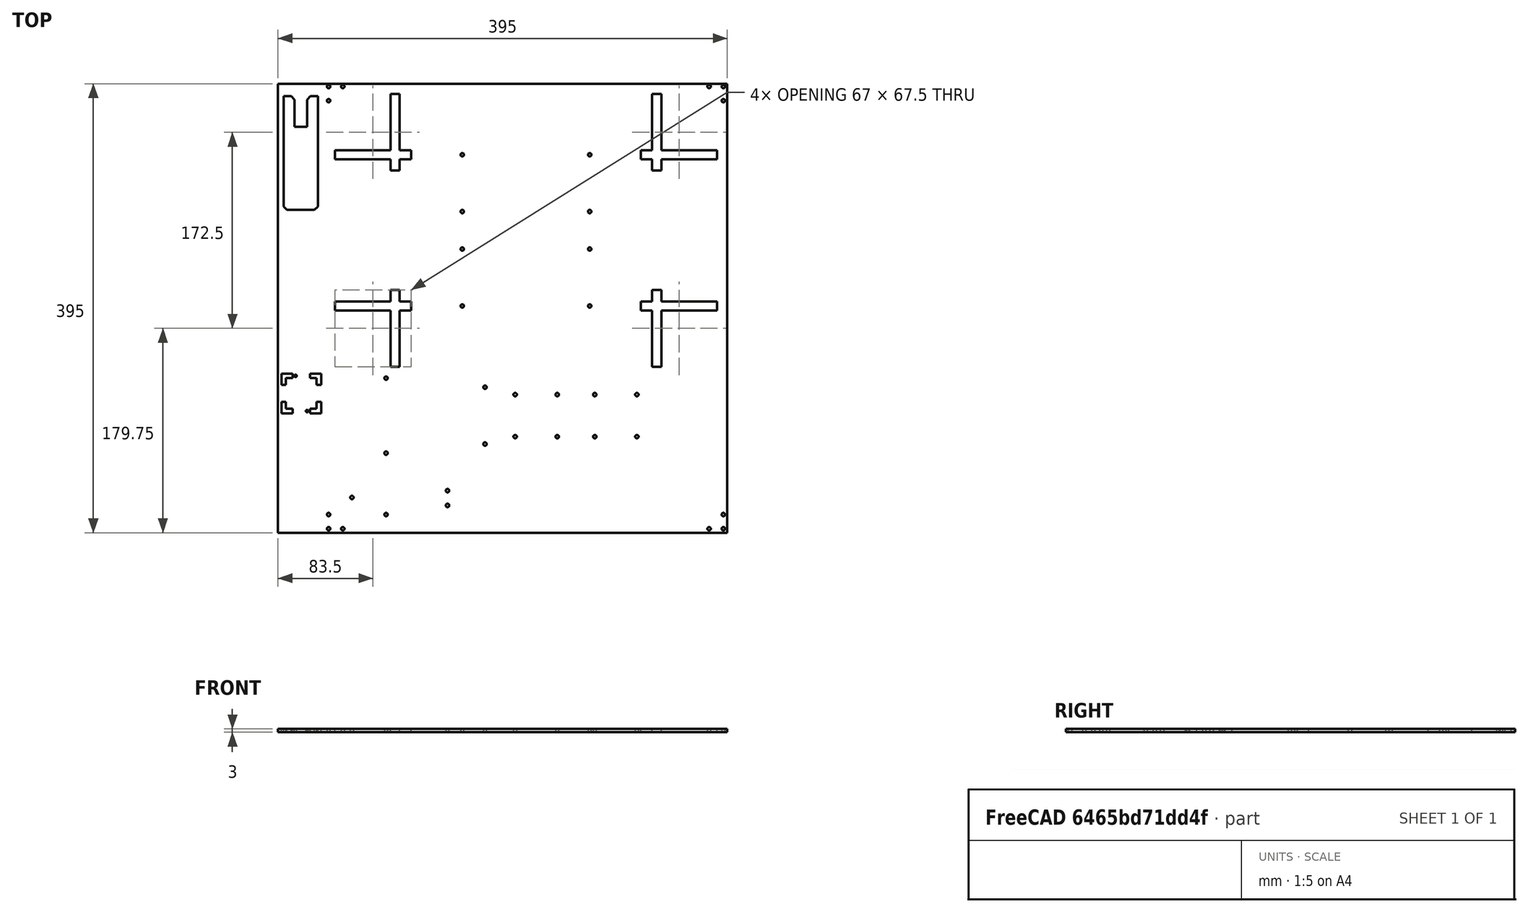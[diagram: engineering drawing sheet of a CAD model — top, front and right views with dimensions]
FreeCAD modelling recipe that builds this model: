
FCSTD DOCUMENT  (FreeCAD 0.19R24291 (Git))
Label: sibi_baseplate
License: All rights reserved
LicenseURL: http://en.wikipedia.org/wiki/All_rights_reserved
objects: Sketcher::SketchObject×1, Spreadsheet::Sheet×1, PartDesign::Pad×1, PartDesign::Body×1, App::Part×1, TechDraw::DrawSVGTemplate×1, TechDraw::DrawViewPart×1, TechDraw::DrawPage×1
note: 4 computed .brp shape members not serialized (recipe doc carries the construction recipe); baked Part::Feature solids carry a one-line shape summary decoded from their .brp

FEATURE [Sketcher::SketchObject] Sketch
  FullyConstrained = true
  MapMode = 5
  Support = -> [XY_Plane001]
  expr: Constraints[9] = <<Value_Spreadsheet>>.baseplate_size
  expr: Constraints[207] = 354.5 - 2.5 - 5
  expr: Constraints[39] = <<Value_Spreadsheet>>.vert_tab_length
  expr: Constraints[40] = <<Value_Spreadsheet>>.hor_tab_length
  expr: Constraints[122] = <<Value_Spreadsheet>>.vert_tab_length
  expr: Constraints[123] = <<Value_Spreadsheet>>.vert_tab_length
  expr: Constraints[121] = <<Value_Spreadsheet>>.hor_tab_length
  expr: Constraints[124] = <<Value_Spreadsheet>>.vert_tab_length
  expr: Constraints[125] = <<Value_Spreadsheet>>.hor_tab_length
  expr: Constraints[126] = <<Value_Spreadsheet>>.hor_tab_length
  sketch-geometry (136):
    g0: LineSegment StartX=-197.5 StartY=197.5 StartZ=0 EndX=197.5 EndY=197.5 EndZ=0
    g1: LineSegment StartX=197.5 StartY=197.5 StartZ=0 EndX=197.5 EndY=-197.5 EndZ=0
    g2: LineSegment StartX=197.5 StartY=-197.5 StartZ=0 EndX=-197.5 EndY=-197.5 EndZ=0
    g3: LineSegment StartX=-197.5 StartY=-197.5 StartZ=0 EndX=-197.5 EndY=197.5 EndZ=0
    g4: LineSegment StartX=-98.5 StartY=188.5 StartZ=0 EndX=-90.5 EndY=188.5 EndZ=0
    g5: LineSegment StartX=-90.5 StartY=188.5 StartZ=0 EndX=-90.5 EndY=139 EndZ=0
    g6: LineSegment StartX=-90.5 StartY=121 StartZ=0 EndX=-98.5 EndY=121 EndZ=0
    g7: LineSegment StartX=-98.5 StartY=121 StartZ=0 EndX=-98.5 EndY=131 EndZ=0
    g8: LineSegment StartX=-147.5 StartY=139 StartZ=0 EndX=-98.5 EndY=139 EndZ=0
    g9: LineSegment StartX=-80.5 StartY=139 StartZ=0 EndX=-80.5 EndY=131 EndZ=0
    g10: LineSegment StartX=-80.5 StartY=131 StartZ=0 EndX=-90.5 EndY=131 EndZ=0
    g11: LineSegment StartX=-147.5 StartY=131 StartZ=0 EndX=-147.5 EndY=139 EndZ=0
    g12: LineSegment StartX=-98.5 StartY=139 StartZ=0 EndX=-98.5 EndY=188.5 EndZ=0
    g13: LineSegment StartX=-90.5 StartY=131 StartZ=0 EndX=-90.5 EndY=121 EndZ=0
    g14: LineSegment StartX=-90.5 StartY=139 StartZ=0 EndX=-80.5 EndY=139 EndZ=0
    g15: LineSegment StartX=-98.5 StartY=131 StartZ=0 EndX=-147.5 EndY=131 EndZ=0
    g16: LineSegment StartX=121.5 StartY=139 StartZ=0 EndX=131.5 EndY=139 EndZ=0
    g17: LineSegment StartX=188.5 StartY=139 StartZ=0 EndX=188.5 EndY=131 EndZ=0
    g18: LineSegment StartX=188.5 StartY=131 StartZ=0 EndX=139.5 EndY=131 EndZ=0
    g19: LineSegment StartX=121.5 StartY=131 StartZ=0 EndX=121.5 EndY=139 EndZ=0
    g20: LineSegment StartX=131.5 StartY=188.5 StartZ=0 EndX=139.5 EndY=188.5 EndZ=0
    g21: LineSegment StartX=139.5 StartY=188.5 StartZ=0 EndX=139.5 EndY=139 EndZ=0
    g22: LineSegment StartX=139.5 StartY=121 StartZ=0 EndX=131.5 EndY=121 EndZ=0
    g23: LineSegment StartX=131.5 StartY=121 StartZ=0 EndX=131.5 EndY=131 EndZ=0
    g24: LineSegment StartX=-98.5 StartY=16 StartZ=0 EndX=-90.5 EndY=16 EndZ=0
    g25: LineSegment StartX=-90.5 StartY=16 StartZ=0 EndX=-90.5 EndY=6 EndZ=0
    g26: LineSegment StartX=-90.5 StartY=-51.5 StartZ=0 EndX=-98.5 EndY=-51.5 EndZ=0
    g27: LineSegment StartX=-98.5 StartY=-51.5 StartZ=0 EndX=-98.5 EndY=-2 EndZ=0
    g28: LineSegment StartX=-80.5 StartY=6 StartZ=0 EndX=-90.5 EndY=6 EndZ=0
    g29: LineSegment StartX=-147.5 StartY=6 StartZ=0 EndX=-147.5 EndY=-2 EndZ=0
    g30: LineSegment StartX=-147.5 StartY=-2 StartZ=0 EndX=-98.5 EndY=-2 EndZ=0
    g31: LineSegment StartX=-80.5 StartY=-2 StartZ=0 EndX=-80.5 EndY=6 EndZ=0
    g32: LineSegment StartX=131.5 StartY=16 StartZ=0 EndX=139.5 EndY=16 EndZ=0
    g33: LineSegment StartX=139.5 StartY=16 StartZ=0 EndX=139.5 EndY=6 EndZ=0
    g34: LineSegment StartX=139.5 StartY=-51.5 StartZ=0 EndX=131.5 EndY=-51.5 EndZ=0
    g35: LineSegment StartX=131.5 StartY=-51.5 StartZ=0 EndX=131.5 EndY=-2 EndZ=0
    g36: LineSegment StartX=121.5 StartY=6 StartZ=0 EndX=131.5 EndY=6 EndZ=0
    g37: LineSegment StartX=188.5 StartY=6 StartZ=0 EndX=188.5 EndY=-2 EndZ=0
    g38: LineSegment StartX=188.5 StartY=-2 StartZ=0 EndX=139.5 EndY=-2 EndZ=0
    g39: LineSegment StartX=121.5 StartY=-2 StartZ=0 EndX=121.5 EndY=6 EndZ=0
    g40: LineSegment StartX=139.5 StartY=139 StartZ=0 EndX=188.5 EndY=139 EndZ=0
    g41: LineSegment StartX=131.5 StartY=139 StartZ=0 EndX=131.5 EndY=188.5 EndZ=0
    g42: LineSegment StartX=131.5 StartY=131 StartZ=0 EndX=121.5 EndY=131 EndZ=0
    g43: LineSegment StartX=139.5 StartY=131 StartZ=0 EndX=139.5 EndY=121 EndZ=0
    g44: LineSegment StartX=139.5 StartY=6 StartZ=0 EndX=188.5 EndY=6 EndZ=0
    g45: LineSegment StartX=131.5 StartY=6 StartZ=0 EndX=131.5 EndY=16 EndZ=0
    g46: LineSegment StartX=131.5 StartY=-2 StartZ=0 EndX=121.5 EndY=-2 EndZ=0
    g47: LineSegment StartX=139.5 StartY=-2 StartZ=0 EndX=139.5 EndY=-51.5 EndZ=0
    g48: LineSegment StartX=-98.5 StartY=6 StartZ=0 EndX=-147.5 EndY=6 EndZ=0
    g49: LineSegment StartX=-98.5 StartY=6 StartZ=0 EndX=-98.5 EndY=16 EndZ=0
    g50: LineSegment StartX=-90.5 StartY=-2 StartZ=0 EndX=-80.5 EndY=-2 EndZ=0
    g51: LineSegment StartX=-90.5 StartY=-2 StartZ=0 EndX=-90.5 EndY=-51.5 EndZ=0
    g52: Circle CenterX=194 CenterY=195 CenterZ=0 NormalX=0 NormalY=0 NormalZ=1 AngleXU=0 Radius=1.5
    g53: Circle CenterX=181.5 CenterY=195 CenterZ=0 NormalX=0 NormalY=0 NormalZ=1 AngleXU=0 Radius=1.5
    g54: Circle CenterX=194 CenterY=182.5 CenterZ=0 NormalX=0 NormalY=0 NormalZ=1 AngleXU=0 Radius=1.5
    g55: Circle CenterX=194 CenterY=-181.5 CenterZ=0 NormalX=0 NormalY=0 NormalZ=1 AngleXU=0 Radius=1.5
    g56: Circle CenterX=194 CenterY=-194 CenterZ=0 NormalX=0 NormalY=0 NormalZ=1 AngleXU=0 Radius=1.5
    g57: Circle CenterX=181.5 CenterY=-194 CenterZ=0 NormalX=0 NormalY=0 NormalZ=1 AngleXU=0 Radius=1.5
    g58: Circle CenterX=-102.5 CenterY=-61.5 CenterZ=0 NormalX=0 NormalY=0 NormalZ=1 AngleXU=0 Radius=1.5
    g59: Circle CenterX=-102.5 CenterY=-127.5 CenterZ=0 NormalX=0 NormalY=0 NormalZ=1 AngleXU=0 Radius=1.5
    g60: Circle CenterX=-15.5 CenterY=-69.5 CenterZ=0 NormalX=0 NormalY=0 NormalZ=1 AngleXU=0 Radius=1.5
    g61: Circle CenterX=-15.5 CenterY=-119.5 CenterZ=0 NormalX=0 NormalY=0 NormalZ=1 AngleXU=0 Radius=1.5
    g62: GeomPoint X=-102.5 Y=-94.5 Z=0
    g63: GeomPoint X=-15.5 Y=-94.5 Z=0
    g64: Circle CenterX=11 CenterY=-76 CenterZ=0 NormalX=0 NormalY=0 NormalZ=1 AngleXU=0 Radius=1.5
    g65: Circle CenterX=11 CenterY=-113 CenterZ=0 NormalX=0 NormalY=0 NormalZ=1 AngleXU=0 Radius=1.5
    g66: Circle CenterX=48 CenterY=-76 CenterZ=0 NormalX=0 NormalY=0 NormalZ=1 AngleXU=0 Radius=1.5
    g67: Circle CenterX=48 CenterY=-113 CenterZ=0 NormalX=0 NormalY=0 NormalZ=1 AngleXU=0 Radius=1.5
    g68: Circle CenterX=81 CenterY=-76 CenterZ=0 NormalX=0 NormalY=0 NormalZ=1 AngleXU=0 Radius=1.5
    g69: Circle CenterX=118 CenterY=-76 CenterZ=0 NormalX=0 NormalY=0 NormalZ=1 AngleXU=0 Radius=1.5
    g70: Circle CenterX=81 CenterY=-113 CenterZ=0 NormalX=0 NormalY=0 NormalZ=1 AngleXU=0 Radius=1.5
    g71: Circle CenterX=118 CenterY=-113 CenterZ=0 NormalX=0 NormalY=0 NormalZ=1 AngleXU=0 Radius=1.5
    g72: GeomPoint X=29.5 Y=-94.5 Z=0
    g73: GeomPoint X=99.5 Y=-94.5 Z=0
    g74: Circle CenterX=-48.5 CenterY=-160.5 CenterZ=0 NormalX=0 NormalY=0 NormalZ=1 AngleXU=0 Radius=1.5
    g75: Circle CenterX=-48.5 CenterY=-173.5 CenterZ=0 NormalX=0 NormalY=0 NormalZ=1 AngleXU=0 Radius=1.5
    g76: Circle CenterX=-153 CenterY=195 CenterZ=0 NormalX=0 NormalY=0 NormalZ=1 AngleXU=0 Radius=1.5
    g77: Circle CenterX=-140.5 CenterY=195 CenterZ=0 NormalX=0 NormalY=0 NormalZ=1 AngleXU=0 Radius=1.5
    g78: Circle CenterX=-153 CenterY=182.5 CenterZ=0 NormalX=0 NormalY=0 NormalZ=1 AngleXU=0 Radius=1.5
    g79: Circle CenterX=-153 CenterY=-194 CenterZ=0 NormalX=0 NormalY=0 NormalZ=1 AngleXU=0 Radius=1.5
    g80: Circle CenterX=-153 CenterY=-181.5 CenterZ=0 NormalX=0 NormalY=0 NormalZ=1 AngleXU=0 Radius=1.5
    g81: Circle CenterX=-140.5 CenterY=-194 CenterZ=0 NormalX=0 NormalY=0 NormalZ=1 AngleXU=0 Radius=1.5
    g82: GeomPoint X=-80.5 Y=135 Z=0
    g83: GeomPoint X=121.5 Y=135 Z=0
    g84: Circle CenterX=-35.5 CenterY=135 CenterZ=0 NormalX=0 NormalY=0 NormalZ=1 AngleXU=0 Radius=1.5
    g85: Circle CenterX=76.5 CenterY=135 CenterZ=0 NormalX=0 NormalY=0 NormalZ=1 AngleXU=0 Radius=1.5
    g86: Circle CenterX=-35.5 CenterY=2 CenterZ=0 NormalX=0 NormalY=0 NormalZ=1 AngleXU=0 Radius=1.5
    g87: Circle CenterX=76.5 CenterY=2 CenterZ=0 NormalX=0 NormalY=0 NormalZ=1 AngleXU=0 Radius=1.5
    g88: GeomPoint X=20.5 Y=135 Z=0
    g89: GeomPoint X=-80.5 Y=2 Z=0
    g90: GeomPoint X=121.5 Y=2 Z=0
    g91: GeomPoint X=20.5 Y=2 Z=0
    g92: LineSegment StartX=-159.5 StartY=-57.5 StartZ=0 EndX=-159.5 EndY=-47.5 EndZ=0
    g93: LineSegment StartX=-159.5 StartY=-47.5 StartZ=0 EndX=-163.5 EndY=-47.5 EndZ=0
    g94: LineSegment StartX=-163.5 StartY=-47.5 StartZ=0 EndX=-163.5 EndY=-61.5 EndZ=0
    g95: LineSegment StartX=-163.5 StartY=-61.5 StartZ=0 EndX=-169.5 EndY=-61.5 EndZ=0
    g96: LineSegment StartX=-169.5 StartY=-61.5 StartZ=0 EndX=-169.5 EndY=-57.5 EndZ=0
    g97: LineSegment StartX=-169.5 StartY=-57.5 StartZ=0 EndX=-159.5 EndY=-57.5 EndZ=0
    g98: LineSegment StartX=-184.5 StartY=-53.5 StartZ=0 EndX=-184.5 EndY=-57.5 EndZ=0
    g99: LineSegment StartX=-184.5 StartY=-57.5 StartZ=0 EndX=-194.5 EndY=-57.5 EndZ=0
    g100: LineSegment StartX=-194.5 StartY=-57.5 StartZ=0 EndX=-194.5 EndY=-47.5 EndZ=0
    g101: LineSegment StartX=-194.5 StartY=-47.5 StartZ=0 EndX=-190.5 EndY=-47.5 EndZ=0
    g102: LineSegment StartX=-190.5 StartY=-47.5 StartZ=0 EndX=-190.5 EndY=-53.5 EndZ=0
    g103: LineSegment StartX=-190.5 StartY=-53.5 StartZ=0 EndX=-184.5 EndY=-53.5 EndZ=0
    g104: LineSegment StartX=-194.5 StartY=-32.5 StartZ=0 EndX=-190.5 EndY=-32.5 EndZ=0
    g105: LineSegment StartX=-190.5 StartY=-32.5 StartZ=0 EndX=-190.5 EndY=-26.5 EndZ=0
    g106: LineSegment StartX=-190.5 StartY=-26.5 StartZ=0 EndX=-184.5 EndY=-26.5 EndZ=0
    g107: LineSegment StartX=-184.5 StartY=-26.5 StartZ=0 EndX=-184.5 EndY=-22.5 EndZ=0
    g108: LineSegment StartX=-184.5 StartY=-22.5 StartZ=0 EndX=-194.5 EndY=-22.5 EndZ=0
    g109: LineSegment StartX=-194.5 StartY=-22.5 StartZ=0 EndX=-194.5 EndY=-32.5 EndZ=0
    g110: LineSegment StartX=-169.5 StartY=-22.5 StartZ=0 EndX=-159.5 EndY=-22.5 EndZ=0
    g111: LineSegment StartX=-159.5 StartY=-22.5 StartZ=0 EndX=-159.5 EndY=-32.5 EndZ=0
    g112: LineSegment StartX=-159.5 StartY=-32.5 StartZ=0 EndX=-163.5 EndY=-32.5 EndZ=0
    g113: LineSegment StartX=-163.5 StartY=-32.5 StartZ=0 EndX=-163.5 EndY=-26.5 EndZ=0
    g114: LineSegment StartX=-163.5 StartY=-26.5 StartZ=0 EndX=-169.5 EndY=-26.5 EndZ=0
    g115: LineSegment StartX=-169.5 StartY=-26.5 StartZ=0 EndX=-169.5 EndY=-22.5 EndZ=0
    g116: Circle CenterX=-172 CenterY=-63.5 CenterZ=0 NormalX=0 NormalY=0 NormalZ=1 AngleXU=0 Radius=1
    g117: Circle CenterX=-182 CenterY=-24.5 CenterZ=0 NormalX=0 NormalY=0 NormalZ=1 AngleXU=0 Radius=1
    g118: Circle CenterX=-35.5 CenterY=85 CenterZ=0 NormalX=0 NormalY=0 NormalZ=1 AngleXU=0 Radius=1.5
    g119: Circle CenterX=-35.5 CenterY=52 CenterZ=0 NormalX=0 NormalY=0 NormalZ=1 AngleXU=0 Radius=1.5
    g120: Circle CenterX=76.5 CenterY=85 CenterZ=0 NormalX=0 NormalY=0 NormalZ=1 AngleXU=0 Radius=1.5
    g121: Circle CenterX=76.5 CenterY=52 CenterZ=0 NormalX=0 NormalY=0 NormalZ=1 AngleXU=0 Radius=1.5
    g122: LineSegment StartX=-192.5 StartY=186.5 StartZ=0 EndX=-192.5 EndY=89.5 EndZ=0
    g123: LineSegment StartX=-192.5 StartY=89.5 StartZ=0 EndX=-189.5 EndY=86.5 EndZ=0
    g124: LineSegment StartX=-189.5 StartY=86.5 StartZ=0 EndX=-165.5 EndY=86.5 EndZ=0
    g125: LineSegment StartX=-165.5 StartY=86.5 StartZ=0 EndX=-162.5 EndY=89.5 EndZ=0
    g126: LineSegment StartX=-162.5 StartY=89.5 StartZ=0 EndX=-162.5 EndY=186.5 EndZ=0
    g127: LineSegment StartX=-162.5 StartY=186.5 StartZ=0 EndX=-169 EndY=186.5 EndZ=0
    g128: LineSegment StartX=-169 StartY=186.5 StartZ=0 EndX=-172 EndY=183.5 EndZ=0
    g129: LineSegment StartX=-172 StartY=183.5 StartZ=0 EndX=-172 EndY=159.5 EndZ=0
    g130: LineSegment StartX=-172 StartY=159.5 StartZ=0 EndX=-183 EndY=159.5 EndZ=0
    g131: LineSegment StartX=-183 StartY=159.5 StartZ=0 EndX=-183 EndY=183.5 EndZ=0
    g132: LineSegment StartX=-183 StartY=183.5 StartZ=0 EndX=-186 EndY=186.5 EndZ=0
    g133: LineSegment StartX=-186 StartY=186.5 StartZ=0 EndX=-192.5 EndY=186.5 EndZ=0
    g134: Circle CenterX=-132.5 CenterY=-166.5 CenterZ=0 NormalX=0 NormalY=0 NormalZ=1 AngleXU=0 Radius=1.5
    g135: Circle CenterX=-102.5 CenterY=-181.5 CenterZ=0 NormalX=0 NormalY=0 NormalZ=1 AngleXU=0 Radius=1.5
  constraints (365):
    c: Coincident(g0,g1)
    c: Coincident(g1,g2)
    c: Coincident(g2,g3)
    c: Coincident(g3,g0)
    c: Horizontal(g0)
    c: Horizontal(g2)
    c: Vertical(g1)
    c: Vertical(g3)
    c: Equal(g0,g3)
    c: DistanceX(g0,g0) = 395
    c: Symmetric(g0,g1,g-1)
    c: Coincident(g4,g5)
    c: Coincident(g13,g6)
    c: Coincident(g6,g7)
    c: Coincident(g12,g4)
    c: Horizontal(g4)
    c: Horizontal(g6)
    c: Vertical(g5)
    c: Vertical(g7)
    c: Coincident(g14,g9)
    c: Coincident(g9,g10)
    c: Coincident(g15,g11)
    c: Coincident(g11,g8)
    c: Horizontal(g8)
    c: Horizontal(g10)
    c: Vertical(g9)
    c: Vertical(g11)
    c: Tangent(g7,g12)
    c: Tangent(g5,g13)
    c: Coincident(g8,g12)
    c: Coincident(g14,g5)
    c: Tangent(g8,g14)
    c: Coincident(g10,g13)
    c: Coincident(g15,g7)
    c: Tangent(g10,g15)
    c: Equal(g13,g10)
    c: DistanceX(g10,g10) = 10
    c: Equal(g6,g9)
    c: DistanceY(g11,g11) = 8
    c: DistanceY(g6,g4) = 67.5
    c: DistanceX(g11,g9) = 67
    c: Coincident(g40,g17)
    c: Coincident(g17,g18)
    c: Coincident(g42,g19)
    c: Coincident(g19,g16)
    c: Horizontal(g16)
    c: Horizontal(g18)
    c: Vertical(g17)
    c: Vertical(g19)
    c: Coincident(g20,g21)
    c: Coincident(g43,g22)
    c: Coincident(g22,g23)
    c: Coincident(g41,g20)
    c: Vertical(g21)
    c: Vertical(g23)
    c: Coincident(g24,g25)
    c: Coincident(g51,g26)
    c: Coincident(g26,g27)
    c: Coincident(g49,g24)
    c: Horizontal(g24)
    c: Horizontal(g26)
    c: Vertical(g25)
    c: Vertical(g27)
    c: Coincident(g48,g29)
    c: Coincident(g29,g30)
    c: Coincident(g50,g31)
    c: Coincident(g31,g28)
    c: Horizontal(g28)
    c: Horizontal(g30)
    c: Coincident(g32,g33)
    c: Coincident(g47,g34)
    c: Coincident(g34,g35)
    c: Coincident(g45,g32)
    c: Vertical(g33)
    c: Vertical(g35)
    c: Coincident(g44,g37)
    c: Coincident(g37,g38)
    c: Coincident(g46,g39)
    c: Coincident(g39,g36)
    c: Horizontal(g36)
    c: Horizontal(g38)
    c: Tangent(g16,g40)
    c: Coincident(g41,g16)
    c: Tangent(g23,g41)
    c: Coincident(g42,g23)
    c: Tangent(g18,g42)
    c: Coincident(g21,g40)
    c: Coincident(g43,g18)
    c: Tangent(g21,g43)
    c: Tangent(g36,g44)
    c: Coincident(g45,g36)
    c: Tangent(g35,g45)
    c: Coincident(g46,g35)
    c: Tangent(g38,g46)
    c: Coincident(g33,g44)
    c: Coincident(g47,g38)
    c: Tangent(g33,g47)
    c: Tangent(g28,g48)
    c: Coincident(g49,g48)
    c: Tangent(g27,g49)
    c: Coincident(g30,g27)
    c: Tangent(g30,g50)
    c: Coincident(g25,g28)
    c: Coincident(g51,g50)
    c: Tangent(g25,g51)
    c: Equal(g13,g25)
    c: Equal(g28,g25)
    c: Equal(g45,g36)
    c: Equal(g45,g10)
    c: Equal(g42,g23)
    c: Equal(g42,g10)
    c: Equal(g9,g19)
    c: Equal(g19,g22)
    c: Equal(g32,g39)
    c: Equal(g22,g32)
    c: Equal(g31,g24)
    c: Equal(g24,g6)
    c: Tangent(g9,g31)
    c: Tangent(g6,g22)
    c: Tangent(g39,g19)
    c: Tangent(g24,g32)
    c: DistanceX(g19,g17) = 67
    c: DistanceY(g22,g20) = 67.5
    c: DistanceY(g34,g32) = 67.5
    c: DistanceY(g26,g24) = 67.5
    c: DistanceX(g29,g28) = 67
    c: DistanceX(g36,g37) = 67
    c: DistanceX(g9,g19) = 202
    c: Vertical(g37)
    c: DistanceY(g24,g6) = 105
    c: Horizontal(g20)
    c: Horizontal(g34)
    c: DistanceX(g0,g17) = -9
    c: Vertical(g29)
    c: DistanceY(g20,g0) = 9
    c: Equal(g53,g52)
    c: Equal(g52,g54)
    c: Diameter(g52) = 3
    c: DistanceY(g53,g52) = 0
    c: DistanceY(g54,g52) = 12.5
    c: DistanceX(g54,g52) = 0
    c: DistanceX(g53,g52) = 12.5
    c: DistanceX(g52,g0) = 3.5
    c: DistanceY(g52,g0) = 2.5
    c: Equal(g57,g56)
    c: Equal(g56,g55)
    c: Equal(g56,g52)
    c: DistanceX(g57,g56) = 12.5
    c: DistanceX(g56,g55) = 0
    c: DistanceY(g57,g56) = 0
    c: DistanceY(g56,g55) = 12.5
    c: DistanceY(g1,g56) = 3.5
    c: DistanceY(g63,g62) = 0
    c: DistanceX(g62,g63) = 87
    c: Symmetric(g58,g59,g62)
    c: Symmetric(g60,g61,g63)
    c: DistanceX(g59,g58) = 0
    c: DistanceX(g60,g61) = 0
    c: DistanceY(g61,g60) = 50
    c: DistanceY(g59,g58) = 66
    c: DistanceY(g2,g59) = 70
    c: DistanceX(g2,g59) = 95
    c: Equal(g58,g59)
    c: Equal(g58,g61)
    c: Equal(g58,g60)
    c: Diameter(g58) = 3
    c: DistanceX(g64,g66) = 37
    c: DistanceX(g65,g64) = 0
    c: DistanceX(g66,g67) = 0
    c: DistanceY(g64,g66) = 0
    c: DistanceY(g67,g65) = 0
    c: DistanceY(g67,g66) = 37
    c: Equal(g64,g66)
    c: Equal(g64,g67)
    c: Equal(g64,g65)
    c: Diameter(g64) = 3
    c: DistanceY(g68,g69) = 0
    c: DistanceY(g71,g70) = 0
    c: DistanceY(g70,g68) = 37
    c: DistanceX(g70,g68) = 0
    c: DistanceX(g71,g69) = 0
    c: DistanceX(g68,g69) = 37
    c: Equal(g64,g68)
    c: Equal(g68,g69)
    c: Equal(g68,g71)
    c: Equal(g68,g70)
    c: Symmetric(g66,g65,g72)
    c: Symmetric(g70,g69,g73)
    c: DistanceY(g73,g72) = 0
    c: DistanceY(g63,g72) = 0
    c: DistanceX(g63,g72) = 45
    c: DistanceX(g72,g73) = 70
    c: DistanceX(g75,g74) = 0
    c: DistanceY(g75,g74) = 13
    c: DistanceY(g2,g75) = 24
    c: DistanceX(g74,g1) = 246
    c: Equal(g74,g75)
    c: Diameter(g74) = 3
    c: Equal(g76,g77)
    c: Equal(g77,g78)
    c: Equal(g76,g52)
    c: DistanceY(g77,g76) = 0
    c: DistanceY(g78,g76) = 12.5
    c: DistanceX(g76,g78) = 0
    c: DistanceX(g76,g77) = 12.5
    c: DistanceX(g52,g56) = 0
    c: DistanceY(g76,g52) = 0
    c: DistanceX(g76,g52) = 347
    c: Equal(g80,g79)
    c: Equal(g79,g81)
    c: Equal(g81,g52)
    c: DistanceX(g80,g79) = 0
    c: DistanceX(g79,g81) = 12.5
    c: DistanceX(g76,g79) = 0
    c: DistanceY(g81,g79) = 0
    c: DistanceY(g79,g80) = 12.5
    c: DistanceY(g56,g79) = 0
    c: Symmetric(g9,g9,g82)
    c: Symmetric(g16,g19,g83)
    c: Equal(g84,g85)
    c: Equal(g85,g86)
    c: Equal(g86,g87)
    c: Equal(g87,g52)
    c: DistanceY(g84,g85) = 0
    c: Symmetric(g83,g82,g88)
    c: Symmetric(g84,g85,g88)
    c: DistanceX(g9,g84) = 45
    c: Symmetric(g28,g31,g89)
    c: Symmetric(g36,g39,g90)
    c: Symmetric(g90,g89,g91)
    c: Symmetric(g86,g87,g91)
    c: DistanceY(g87,g86) = 0
    c: DistanceX(g86,g84) = 0
    c: Vertical(g92)
    c: Coincident(g92,g93)
    c: Horizontal(g93)
    c: Coincident(g93,g94)
    c: Vertical(g94)
    c: Coincident(g94,g95)
    c: Horizontal(g95)
    c: Coincident(g95,g96)
    c: Vertical(g96)
    c: Coincident(g96,g97)
    c: Coincident(g97,g92)
    c: Horizontal(g97)
    c: DistanceX(g93,g93) = 4
    c: Equal(g96,g93)
    c: DistanceY(g92,g92) = 10
    c: Equal(g97,g92)
    c: DistanceY(g2,g96) = 140
    c: DistanceX(g2,g92) = 38
    c: Vertical(g98)
    c: Coincident(g98,g99)
    c: Horizontal(g99)
    c: Coincident(g99,g100)
    c: Vertical(g100)
    c: Coincident(g100,g101)
    c: Horizontal(g101)
    c: Coincident(g101,g102)
    c: Vertical(g102)
    c: Coincident(g102,g103)
    c: Coincident(g103,g98)
    c: Horizontal(g103)
    c: Equal(g101,g93)
    c: Equal(g99,g92)
    c: Equal(g100,g99)
    c: Equal(g101,g98)
    c: DistanceY(g92,g99) = 0
    c: DistanceX(g99,g92) = 35
    c: Horizontal(g104)
    c: Coincident(g104,g105)
    c: Vertical(g105)
    c: Coincident(g105,g106)
    c: Horizontal(g106)
    c: Coincident(g106,g107)
    c: Vertical(g107)
    c: Coincident(g107,g108)
    c: Horizontal(g108)
    c: Coincident(g108,g109)
    c: Coincident(g109,g104)
    c: Vertical(g109)
    c: Equal(g109,g92)
    c: Equal(g108,g92)
    c: Equal(g93,g104)
    c: Equal(g93,g107)
    c: DistanceX(g108,g99) = 0
    c: DistanceY(g99,g108) = 35
    c: Horizontal(g110)
    c: Coincident(g110,g111)
    c: Vertical(g111)
    c: Coincident(g111,g112)
    c: Horizontal(g112)
    c: Coincident(g112,g113)
    c: Vertical(g113)
    c: Coincident(g113,g114)
    c: Horizontal(g114)
    c: Coincident(g114,g115)
    c: Coincident(g115,g110)
    c: Vertical(g115)
    c: Equal(g112,g93)
    c: Equal(g115,g93)
    c: Equal(g111,g92)
    c: Equal(g92,g110)
    c: DistanceX(g92,g110) = 0
    c: DistanceY(g108,g110) = 0
    c: DistanceY(g116,g95) = 2
    c: DistanceX(g116,g95) = 2.5
    c: Diameter(g116) = 2
    c: Diameter(g117) = 2
    c: DistanceY(g117,g107) = 2
    c: DistanceX(g107,g117) = 2.5
    c: Diameter(g118) = 3
    c: Equal(g119,g118)
    c: Equal(g121,g118)
    c: Equal(g120,g118)
    c: DistanceX(g118,g84) = 0
    c: DistanceX(g119,g118) = 0
    c: DistanceY(g118,g84) = 50
    c: DistanceY(g86,g119) = 50
    c: DistanceY(g121,g119) = 0
    c: DistanceY(g118,g120) = 0
    c: DistanceX(g121,g87) = 0
    c: DistanceX(g120,g121) = 0
    c: Vertical(g122)
    c: Coincident(g122,g123)
    c: Coincident(g123,g124)
    c: Horizontal(g124)
    c: Coincident(g124,g125)
    c: Coincident(g125,g126)
    c: Vertical(g126)
    c: Coincident(g126,g127)
    c: Horizontal(g127)
    c: Coincident(g127,g128)
    c: Coincident(g128,g129)
    c: Vertical(g129)
    c: Coincident(g129,g130)
    c: Horizontal(g130)
    c: Coincident(g130,g131)
    c: Vertical(g131)
    c: Coincident(g131,g132)
    c: Coincident(g132,g133)
    c: Coincident(g133,g122)
    c: Horizontal(g133)
    c: DistanceY(g122,g0) = 11
    c: DistanceX(g0,g122) = 5
    c: DistanceX(g133,g133) = 6.5
    c: Equal(g133,g127)
    c: DistanceY(g122,g122) = 97
    c: Equal(g122,g126)
    c: DistanceY(g122,g126) = 0
    c: DistanceX(g124,g124) = 24
    c: Equal(g125,g123)
    c: DistanceY(g123,g122) = 3
    c: Equal(g132,g128)
    c: DistanceY(g131,g131) = 24
    c: Equal(g131,g129)
    c: DistanceX(g130,g130) = 11
    c: DistanceX(g122,g126) = 30
    c: DistanceY(g128,g127) = 3
    c: Diameter(g134) = 3
    c: Equal(g134,g135)
    c: DistanceX(g134,g135) = 30
    c: DistanceY(g135,g134) = 15
    c: DistanceX(g59,g135) = 0
    c: DistanceY(g80,g135) = 0
FEATURE [Spreadsheet::Sheet] Spreadsheet  label="Value_Spreadsheet"
  cells = A2=Baseplate Width; B2(baseplate_size)=395; A5=Horizontal Tab; B5(hor_tab_length)=67; A6=Vertical Tab; B6(vert_tab_length)=67.5
FEATURE [PartDesign::Pad] Pad
  Direction = (1,1,1)
  Length = 3
  Length2 = 100
  Profile = -> Sketch
  Refine = true
  Type = 0
FEATURE [PartDesign::Body] Body
  Group = -> [Sketch,Pad]
  Origin = -> Origin001
  Placement = pos=(200,-200,0) rot=(0,0,1;0rad)
  Tip = -> Pad
FEATURE [App::Part] Part
  Group = -> [Body]
  Origin = -> Origin
FEATURE [TechDraw::DrawSVGTemplate] Template
  Height = 420
  Orientation = 1
  Width = 594
FEATURE [TechDraw::DrawViewPart] View
  CoarseView = false
  Direction = (0,0,1)
  Focus = 100
  HardHidden = false
  IsoCount = 0
  IsoHidden = false
  IsoVisible = false
  LockPosition = false
  Perspective = false
  Rotation = 0
  ScaleType = 0
  SeamHidden = false
  SeamVisible = true
  SmoothHidden = false
  SmoothVisible = true
  Source = -> [Sketch]
  X = 297
  XDirection = (1,0,0)
  Y = 210
FEATURE [TechDraw::DrawPage] Page
  KeepUpdated = true
  NextBalloonIndex = 1
  ProjectionType = 0
  Template = -> Template
  Views = -> [View]
